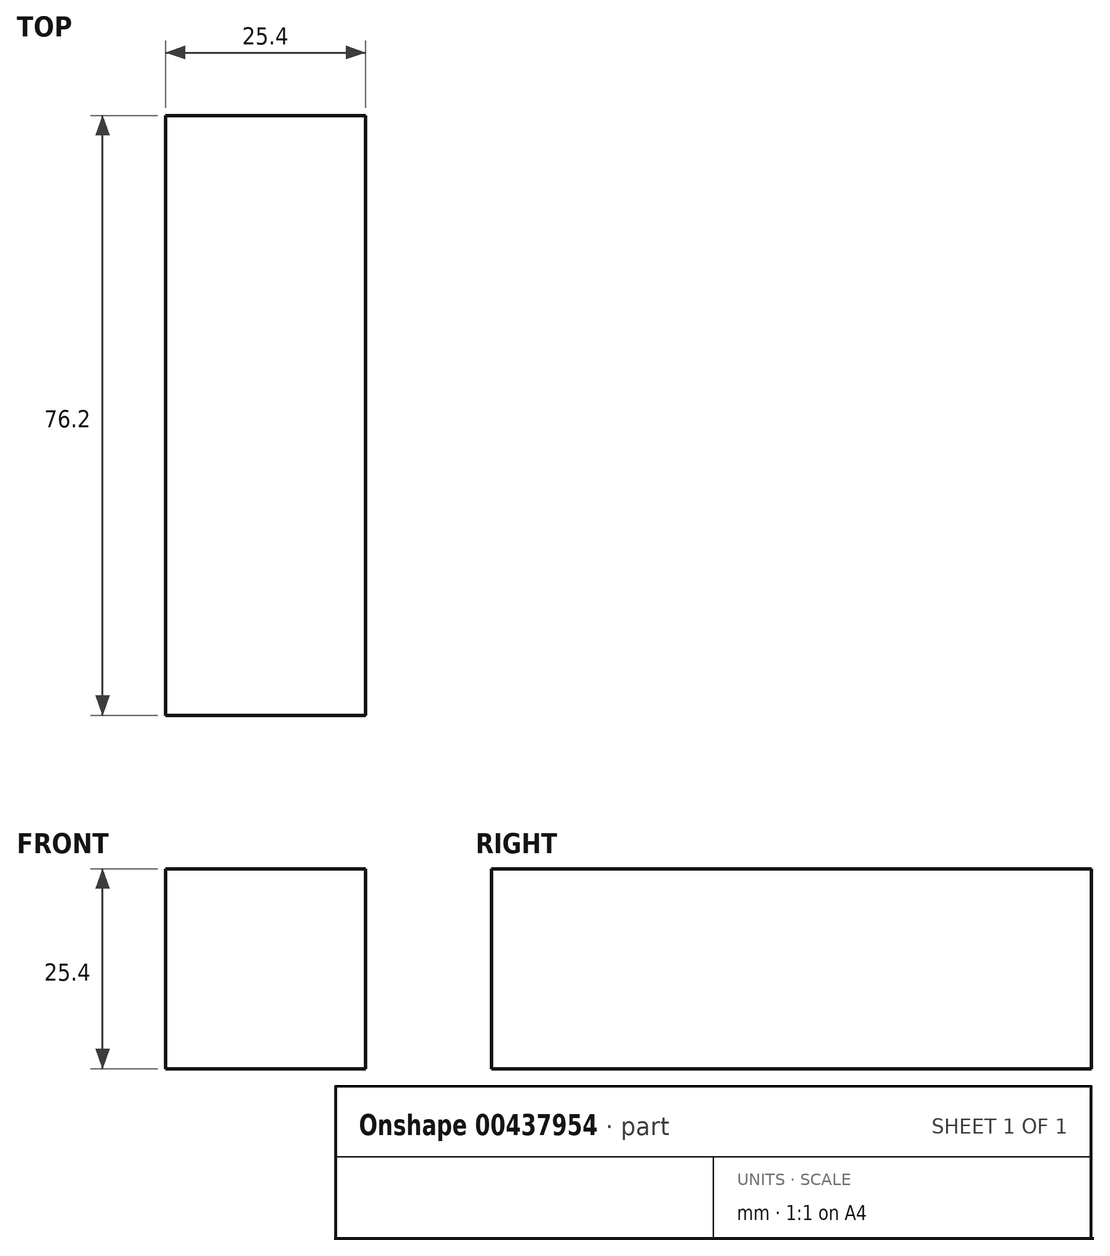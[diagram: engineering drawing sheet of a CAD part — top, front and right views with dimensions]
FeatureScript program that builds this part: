
annotation { "Feature Type Name" : "Feature", "Feature Type Description" : "" }
export const myFeature = defineFeature(function(context is Context, id is Id, definition is map)
    precondition{}
    {
        {
            var Q0;
            Q0=qCreatedBy(makeId("Front.planeOp"),FACE);
            var sketch = newSketch(context, id + "F0", { "sketchPlane" : qUnion([Q0])});
            skLineSegment(sketch, "E0.bottom", {"start": v(-54.62, 53.09) * mm, "end": v(-29.22, 53.09) * mm});
            skLineSegment(sketch, "E0.top", {"start": v(-54.62, 27.69) * mm, "end": v(-29.22, 27.69) * mm});
            skLineSegment(sketch, "E0.left", {"start": v(-54.62, 53.09) * mm, "end": v(-54.62, 27.69) * mm});
            skLineSegment(sketch, "E0.right", {"start": v(-29.22, 53.09) * mm, "end": v(-29.22, 27.69) * mm});
            skSolve(sketch);
        }
        {
            var Q0;
            Q0=makeQuery(id+"F0.imprint","IMPRINT",FACE,{"disambiguationData":[TD([[makeQuery(id+"F0.imprint","IMPRINT",EDGE,{"derivedFrom":sQuery(id+"F0.wireOp",EDGE,"E0.bottom")}),-1.0]])]});
            extrude(context, id + "F1", {"entities" : qUnion([Q0]), "depth" : 76.2 * mm});
        }
    });
